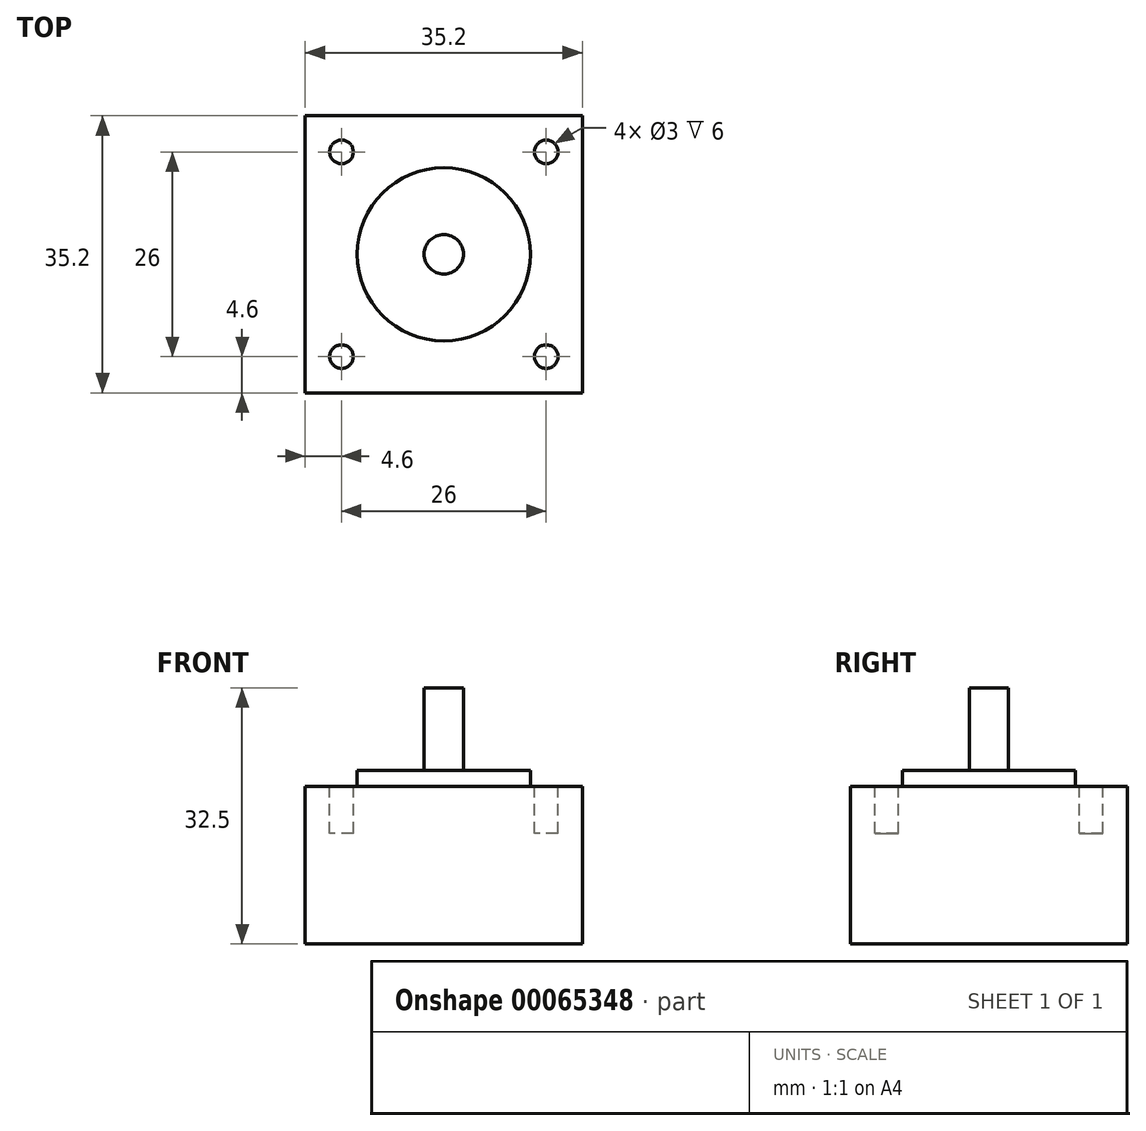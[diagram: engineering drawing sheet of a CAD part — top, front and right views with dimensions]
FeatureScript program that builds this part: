
annotation { "Feature Type Name" : "Feature", "Feature Type Description" : "" }
export const myFeature = defineFeature(function(context is Context, id is Id, definition is map)
    precondition{}
    {
        {
            var Q0;
            Q0=qCreatedBy(makeId("Top.planeOp"),FACE);
            var sketch = newSketch(context, id + "F0", { "sketchPlane" : qUnion([Q0])});
            skLineSegment(sketch, "E0.rect.bottom", {"start": v(-17.6, 17.6) * mm, "end": v(17.6, 17.6) * mm});
            skLineSegment(sketch, "E0.rect.top", {"start": v(-17.6, -17.6) * mm, "end": v(17.6, -17.6) * mm});
            skLineSegment(sketch, "E0.rect.left", {"start": v(-17.6, 17.6) * mm, "end": v(-17.6, -17.6) * mm});
            skLineSegment(sketch, "E0.rect.right", {"start": v(17.6, 17.6) * mm, "end": v(17.6, -17.6) * mm});
            skPoint(sketch, "E0.rect.middle", {"position": v(0, 0) * mm});
            skLineSegment(sketch, "E1", {"start": v(17.6, -17.6) * mm, "end": v(-17.6, 17.6) * mm, "construction": true});
            skSolve(sketch);
        }
        {
            var Q0;
            Q0=qSketchRegion(id+"F0",true);
            extrude(context, id + "F1", {"entities" : qUnion([Q0]), "depth" : 20 * mm});
        }
        {
            var Q0;
            Q0=makeQuery(id+"F1.opExtrude","CAP_FACE",FACE,{"disambiguationData":[OSD([sQuery(id+"F0.wireOp",EDGE,"E0.rect.bottom"),sQuery(id+"F0.wireOp",EDGE,"E0.rect.top"),sQuery(id+"F0.wireOp",EDGE,"E0.rect.left"),sQuery(id+"F0.wireOp",EDGE,"E0.rect.right")])],"isStart":false});
            var sketch = newSketch(context, id + "F2", { "sketchPlane" : qUnion([Q0])});
            skCircle(sketch, "E2", {"center": v(0, 0) * mm, "radius": 11 * mm});
            skSolve(sketch);
        }
        {
            var Q0;
            Q0=qSketchRegion(id+"F2",true);
            extrude(context, id + "F3", {"entities" : qUnion([Q0]), "operationType" : NewBodyOperationType.ADD, "depth" : 2 * mm});
        }
        {
            var Q0;
            Q0=makeQuery(id+"F1.opExtrude","CAP_FACE",FACE,{"disambiguationData":[OSD([sQuery(id+"F0.wireOp",EDGE,"E0.rect.bottom"),sQuery(id+"F0.wireOp",EDGE,"E0.rect.top"),sQuery(id+"F0.wireOp",EDGE,"E0.rect.left"),sQuery(id+"F0.wireOp",EDGE,"E0.rect.right")])],"isStart":false});
            var sketch = newSketch(context, id + "F4", { "sketchPlane" : qUnion([Q0])});
            skCircle(sketch, "E3", {"center": v(0, 0) * mm, "radius": 2.5 * mm});
            skSolve(sketch);
        }
        {
            var Q0;
            Q0=makeQuery(id+"F4.imprint","IMPRINT",FACE,{"disambiguationData":[TD([[makeQuery(id+"F4.imprint","IMPRINT",EDGE,{"derivedFrom":sQuery(id+"F4.wireOp",EDGE,"E3")}),1.0]])]});
            extrude(context, id + "F5", {"entities" : qUnion([Q0]), "operationType" : NewBodyOperationType.ADD, "depth" : 12.5 * mm});
        }
        {
            var Q0;
            Q0=makeQuery(id+"F1.opExtrude","CAP_FACE",FACE,{"disambiguationData":[OSD([sQuery(id+"F0.wireOp",EDGE,"E0.rect.bottom"),sQuery(id+"F0.wireOp",EDGE,"E0.rect.top"),sQuery(id+"F0.wireOp",EDGE,"E0.rect.left"),sQuery(id+"F0.wireOp",EDGE,"E0.rect.right")])],"isStart":false});
            var sketch = newSketch(context, id + "F6", { "sketchPlane" : qUnion([Q0])});
            skCircle(sketch, "E4", {"center": v(-13, 13) * mm, "radius": 1.5 * mm});
            skCircle(sketch, "E5.MirrorC", {"center": v(13, 13) * mm, "radius": 1.5 * mm});
            skCircle(sketch, "E6.MirrorC", {"center": v(-13, -13) * mm, "radius": 1.5 * mm});
            skCircle(sketch, "E7.MirrorC", {"center": v(13, -13) * mm, "radius": 1.5 * mm});
            skLineSegment(sketch, "E8", {"start": v(-13, 13) * mm, "end": v(13, -13) * mm, "construction": true});
            skLineSegment(sketch, "E9.rect.bottom", {"start": v(-13, 13) * mm, "end": v(13, 13) * mm, "construction": true});
            skLineSegment(sketch, "E9.rect.top", {"start": v(-13, -13) * mm, "end": v(13, -13) * mm, "construction": true});
            skLineSegment(sketch, "E9.rect.left", {"start": v(-13, 13) * mm, "end": v(-13, -13) * mm, "construction": true});
            skLineSegment(sketch, "E9.rect.right", {"start": v(13, 13) * mm, "end": v(13, -13) * mm, "construction": true});
            skPoint(sketch, "E9.rect.middle", {"position": v(0, 0) * mm});
            skSolve(sketch);
        }
        {
            var Q0;
            Q0=qSketchRegion(id+"F6",true);
            extrude(context, id + "F7", {"entities" : qUnion([Q0]), "operationType" : NewBodyOperationType.REMOVE, "oppositeDirection" : true, "depth" : 6 * mm});
        }
    });
